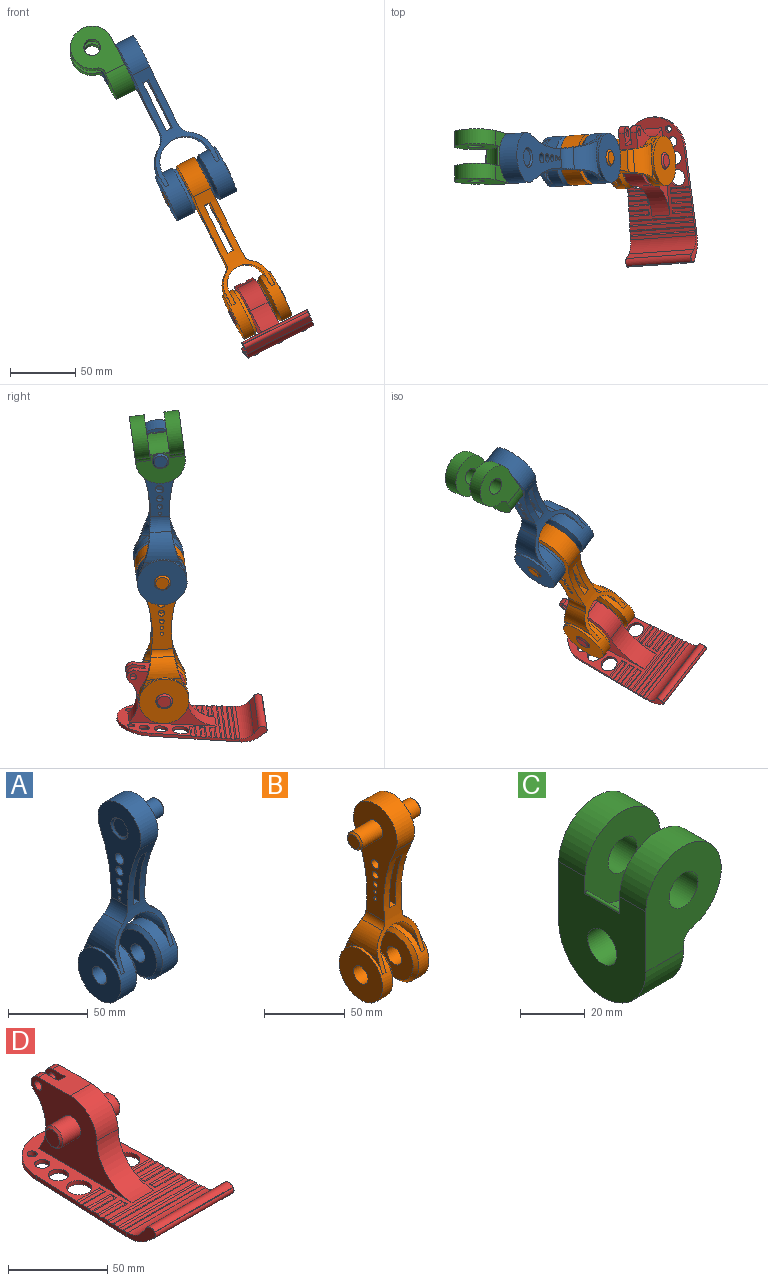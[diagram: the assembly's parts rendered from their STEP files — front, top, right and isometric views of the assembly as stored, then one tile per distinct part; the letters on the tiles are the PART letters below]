
ASSEMBLY  parts=4 mates=3
PART A: 47 faces, bbox 52.1x38.2x142.3 mm
  f0: cylinder r=101.6mm len=87.7mm, axis (-1,0,0), area 964.8mm2, adj f2,f3,f4,f5,f7,f12,f13,f14
  f1: cylinder r=101.6mm len=87.7mm, axis (-1,0,0), area 964.4mm2, adj f2,f3,f4,f5,f8,f9,f10,f11
  f2: cylinder r=23.61mm len=27.14mm, axis (0,1,0), area 470mm2, adj f0,f1,f5,f7,f11,f46
  f3: cylinder r=20.32mm len=40.64mm, axis (0,1,0), area 1216.7mm2, adj f0,f1,f5,f8,f9,f12,f13,f17
  f4: cylinder r=23.61mm len=27.14mm, axis (0,1,0), area 470mm2, adj f0,f1,f10,f14,f17,f45
  f5: cylinder r=19.05mm len=38.1mm, axis (-1,0,0), area 1536.5mm2, adj f0,f1,f2,f3,f7,f8,f11,f12
  f6: cylinder r=6.35mm len=16.51mm, axis (1,0,0), area 658.7mm2, adj f19,f21
  f7: plane 8.59x8.17mm, normal (-1,0,-0.04), area 11.2mm2, adj f0,f2,f5
  f8: plane 10.35x9.56mm, normal (1,0,0), area 16.7mm2, adj f1,f3,f5
  f9: plane 10.35x9.56mm, normal (-1,0,0), area 16.7mm2, adj f1,f3,f17
  f10: plane 8.59x8.17mm, normal (1,0,-0.04), area 11.2mm2, adj f1,f4,f17
  f11: plane 8.59x8.17mm, normal (-1,0,-0.04), area 11.2mm2, adj f1,f2,f5
  f12: plane 10.35x9.56mm, normal (1,0,0), area 16.7mm2, adj f0,f3,f5
  f13: plane 10.35x9.56mm, normal (-1,0,0), area 16.7mm2, adj f0,f3,f17
  f14: plane 8.59x8.17mm, normal (1,0,-0.04), area 11.2mm2, adj f0,f4,f17
  f15: plane 75.32x38.1mm, normal (1,0,0), area 1613mm2, adj f0,f1,f25,f26,f35,f36,f37,f38
  f16: plane 75.32x38.1mm, normal (-1,0,0), area 1557.2mm2, adj f0,f1,f25,f34,f40,f41,f42,f43
  f17: cylinder r=19.05mm len=38.1mm, axis (-1,0,0), area 1536.5mm2, adj f0,f1,f3,f4,f9,f10,f13,f14
  f18: plane 38.1x38.1mm, normal (1,0,0), area 1013.4mm2, adj f17,f20
  f19: plane 38.1x38.1mm, normal (-1,0,0), area 1013.4mm2, adj f5,f6
  f20: cylinder r=6.35mm len=16.51mm, axis (1,0,0), area 658.7mm2, adj f18,f22
  f21: plane 33.02x33.02mm, normal (1,0,0), area 729.7mm2, adj f6,f24
  f22: plane 33.02x33.02mm, normal (-1,0,0), area 729.7mm2, adj f20,f23
  f23: cone r=19.05mm half-angle=45deg, axis (1,0,0), area 401.3mm2, adj f17,f22
  f24: cone r=16.51mm half-angle=45deg, axis (-1,0,0), area 401.3mm2, adj f5,f21
  f25: cylinder r=19.05mm len=38.1mm, axis (-1,0,0), area 1171.2mm2, adj f0,f1,f15,f16
  f26: cylinder r=6.35mm len=17.78mm, axis (-1,0,0), area 709.4mm2, adj f15,f28
  f27: plane 10.16x10.16mm, normal (1,0,0), area 81.1mm2, adj f28
  f28: cone r=5.08mm half-angle=45deg, axis (-1,0,0), area 64.5mm2, adj f26,f27
  f29: plane 27.04x5.08mm, normal (0,0,-1), area 137.4mm2, adj f0,f1,f30,f32
  f30: plane 40.64x27.04mm, normal (1,0,0), area 620.1mm2, adj f0,f1,f29,f31,f40,f41,f42,f43
  f31: plane 14.77x5.08mm, normal (0,0,1), area 75mm2, adj f0,f1,f30,f32
  f32: plane 40.64x27.04mm, normal (-1,0,0), area 620.1mm2, adj f0,f1,f29,f31,f35,f36,f37,f38
  f33: plane 12.7x12.7mm, normal (-1,0,0), area 126.7mm2, adj f34
  f34: cone r=6.35mm half-angle=45deg, axis (-1,0,0), area 78.8mm2, adj f16,f33
  f35: cylinder r=2.54mm len=5.08mm, axis (1,0,0), area 81.1mm2, adj f15,f32
  f36: cylinder r=1.91mm len=5.08mm, axis (1,0,0), area 60.8mm2, adj f15,f32
  f37: cylinder r=1.27mm len=5.08mm, axis (1,0,0), area 40.5mm2, adj f15,f32
  f38: cylinder r=3.17mm len=6.35mm, axis (1,0,0), area 101.3mm2, adj f15,f32
  f39: cylinder r=3.81mm len=7.62mm, axis (1,0,0), area 121.6mm2, adj f15,f32
  f40: cylinder r=2.54mm len=5.08mm, axis (1,0,0), area 81.1mm2, adj f16,f30
  f41: cylinder r=1.91mm len=5.08mm, axis (1,0,0), area 60.8mm2, adj f16,f30
  f42: cylinder r=1.27mm len=5.08mm, axis (1,0,0), area 40.5mm2, adj f16,f30
  f43: cylinder r=3.17mm len=6.35mm, axis (1,0,0), area 101.3mm2, adj f16,f30
  f44: cylinder r=3.81mm len=7.62mm, axis (1,0,0), area 121.6mm2, adj f16,f30
  f45: cylinder r=12.7mm len=16.62mm, axis (0,1,0), area 192.8mm2, adj f0,f1,f4,f15
  f46: cylinder r=12.7mm len=16.62mm, axis (0,1,0), area 192.8mm2, adj f0,f1,f2,f16
PART B: 48 faces, bbox 53.3x38.1x142.2 mm
  f0: cylinder r=101.6mm len=87.7mm, axis (-1,0,0), area 975.1mm2, adj f2,f3,f4,f5,f6,f7,f13,f14
  f1: cylinder r=101.6mm len=87.7mm, axis (-1,0,0), area 974.7mm2, adj f2,f3,f4,f5,f6,f7,f9,f10
  f2: cylinder r=15.24mm len=30.48mm, axis (0,1,0), area 970.1mm2, adj f0,f1,f7,f9,f10,f13,f14,f19
  f3: cylinder r=18.41mm len=26.39mm, axis (0,1,0), area 372.4mm2, adj f0,f1,f5,f11,f15,f19
  f4: cylinder r=18.41mm len=26.39mm, axis (0,1,0), area 372.4mm2, adj f0,f1,f6,f7,f12,f18
  f5: cylinder r=6.35mm len=18.09mm, axis (0,1,0), area 106.3mm2, adj f0,f1,f3,f16
  f6: cylinder r=6.35mm len=18.09mm, axis (0,1,0), area 106.3mm2, adj f0,f1,f4,f17
  f7: cylinder r=19.05mm len=38.1mm, axis (-1,0,0), area 927.7mm2, adj f0,f1,f2,f4,f9,f12,f13,f18
  f8: cylinder r=6.35mm len=12.7mm, axis (1,0,0), area 456mm2, adj f21,f23
  f9: plane 10.35x9.56mm, normal (1,0,0), area 16.7mm2, adj f1,f2,f7
  f10: plane 10.35x9.56mm, normal (-1,0,0), area 16.7mm2, adj f1,f2,f19
  f11: plane 10.35x9.56mm, normal (1,0,0), area 16.7mm2, adj f1,f3,f19
  f12: plane 10.35x9.56mm, normal (-1,0,0), area 16.7mm2, adj f1,f4,f7
  f13: plane 10.35x9.56mm, normal (1,0,0), area 16.7mm2, adj f0,f2,f7
  f14: plane 10.35x9.56mm, normal (-1,0,0), area 16.7mm2, adj f0,f2,f19
  f15: plane 10.35x9.56mm, normal (1,0,0), area 16.7mm2, adj f0,f3,f19
  f16: plane 84.96x38.1mm, normal (1,0,0), area 1801.6mm2, adj f0,f1,f5,f27,f28,f37,f38,f39
  f17: plane 84.96x38.1mm, normal (-1,0,0), area 1801.6mm2, adj f0,f1,f6,f27,f35,f42,f43,f44
  f18: plane 10.35x9.56mm, normal (-1,0,0), area 16.7mm2, adj f0,f4,f7
  f19: cylinder r=19.05mm len=38.1mm, axis (-1,0,0), area 927.7mm2, adj f0,f1,f2,f3,f10,f11,f14,f15
  f20: plane 38.1x38.1mm, normal (1,0,0), area 1013.4mm2, adj f19,f22
  f21: plane 38.1x38.1mm, normal (-1,0,0), area 1013.4mm2, adj f7,f8
  f22: cylinder r=6.35mm len=12.7mm, axis (1,0,0), area 456mm2, adj f20,f24
  f23: plane 33.02x33.02mm, normal (1,0,0), area 729.7mm2, adj f8,f26
  f24: plane 33.02x33.02mm, normal (-1,0,0), area 729.7mm2, adj f22,f25
  f25: cone r=19.05mm half-angle=45deg, axis (1,0,0), area 401.3mm2, adj f19,f24
  f26: cone r=16.51mm half-angle=45deg, axis (-1,0,0), area 401.3mm2, adj f7,f23
  f27: cylinder r=19.05mm len=38.1mm, axis (-1,0,0), area 1171.2mm2, adj f0,f1,f16,f17
  f28: cylinder r=6.35mm len=17.78mm, axis (-1,0,0), area 709.4mm2, adj f16,f30
  f29: plane 10.16x10.16mm, normal (1,0,0), area 81.1mm2, adj f30
  f30: cone r=5.08mm half-angle=45deg, axis (-1,0,0), area 64.5mm2, adj f28,f29
  f31: plane 26.39x5.08mm, normal (0,0,-1), area 134.1mm2, adj f0,f1,f32,f34
  f32: plane 40.64x26.39mm, normal (1,0,0), area 650.1mm2, adj f0,f1,f31,f33,f42,f43,f44,f45
  f33: plane 14.87x5.08mm, normal (0,0,1), area 75.5mm2, adj f0,f1,f32,f34
  f34: plane 40.64x26.39mm, normal (-1,0,0), area 650.1mm2, adj f0,f1,f31,f33,f37,f38,f39,f40
  f35: cylinder r=6.35mm len=17.78mm, axis (1,0,0), area 709.4mm2, adj f17,f47
  f36: plane 10.16x10.16mm, normal (-1,0,0), area 81.1mm2, adj f47
  f37: cylinder r=1.91mm len=5.08mm, axis (1,0,0), area 60.8mm2, adj f16,f34
  f38: cylinder r=1.27mm len=5.08mm, axis (1,0,0), area 40.5mm2, adj f16,f34
  f39: cylinder r=1.27mm len=5.08mm, axis (1,0,0), area 40.5mm2, adj f16,f34
  f40: cylinder r=2.54mm len=5.08mm, axis (1,0,0), area 81.1mm2, adj f16,f34
  f41: cylinder r=3.17mm len=6.35mm, axis (1,0,0), area 101.3mm2, adj f16,f34
  f42: cylinder r=1.91mm len=5.08mm, axis (1,0,0), area 60.8mm2, adj f17,f32
  f43: cylinder r=1.27mm len=5.08mm, axis (1,0,0), area 40.5mm2, adj f17,f32
  f44: cylinder r=1.27mm len=5.08mm, axis (1,0,0), area 40.5mm2, adj f17,f32
  f45: cylinder r=2.54mm len=5.08mm, axis (1,0,0), area 81.1mm2, adj f17,f32
  f46: cylinder r=3.17mm len=6.35mm, axis (1,0,0), area 101.3mm2, adj f17,f32
  f47: cone r=5.08mm half-angle=45deg, axis (1,0,0), area 64.5mm2, adj f35,f36
PART C: 20 faces, bbox 33x38.1x58.4 mm
  f0: cylinder r=6.35mm len=12.7mm, axis (0,1,0), area 456mm2, adj f4,f11
  f1: cylinder r=16.51mm len=33.02mm, axis (0,1,0), area 844.4mm2, adj f4,f6,f11,f13
  f2: plane 38.1x24.9mm, normal (1,0,0), area 577.1mm2, adj f3,f4,f5,f7,f11,f12,f13,f14
  f3: cylinder r=19.05mm len=38.1mm, axis (-1,0,0), area 988.1mm2, adj f2,f4,f5,f6
  f4: plane 39.37x33.02mm, normal (0,1,0), area 896.7mm2, adj f0,f1,f2,f3,f6,f13
  f5: plane 39.37x33.02mm, normal (0,-1,0), area 896.7mm2, adj f2,f3,f6,f8,f9,f14
  f6: plane 41.91x38.1mm, normal (-1,0,0), area 1215.6mm2, adj f1,f3,f4,f5,f7,f9,f11,f12
  f7: cylinder r=6.35mm len=16.51mm, axis (1,0,0), area 658.7mm2, adj f2,f6,f15,f18
  f8: cylinder r=6.35mm len=12.7mm, axis (0,1,0), area 456mm2, adj f5,f12
  f9: cylinder r=16.51mm len=33.02mm, axis (0,1,0), area 844.4mm2, adj f5,f6,f12,f14
  f10: cylinder r=16.51mm len=15.29mm, axis (0,-1,0), area 291.5mm2, adj f11,f12,f15,f16,f17,f18,f19
  f11: plane 37.49x33.02mm, normal (0,-1,0), area 735.6mm2, adj f0,f1,f2,f6,f10,f13,f17,f19
  f12: plane 37.49x33.02mm, normal (0,1,0), area 735.6mm2, adj f2,f6,f8,f9,f10,f14,f16,f19
  f13: cylinder r=5.08mm len=11.43mm, axis (0,1,0), area 77.4mm2, adj f1,f2,f4,f11
  f14: cylinder r=5.08mm len=11.43mm, axis (0,1,0), area 77.4mm2, adj f2,f5,f9,f12
  f15: bspline ~2.72x0.6mm, area 0.6mm2, adj f7,f10,f16
  f16: cylinder r=0.51mm len=5.15mm, axis (0,-1,0), area 4mm2, adj f2,f10,f12,f15
  f17: cylinder r=0.51mm len=5.15mm, axis (0,-1,0), area 4mm2, adj f2,f10,f11,f18
  f18: bspline ~2.72x0.6mm, area 0.6mm2, adj f7,f10,f17
  f19: cylinder r=0.64mm len=15.24mm, axis (0,-1,0), area 26.7mm2, adj f6,f10,f11,f12
PART D: 97 faces, bbox 55.9x113x47.5 mm
  f0: plane 77.94x54.68mm, normal (0,0,1), area 2114.6mm2, adj f4,f8,f9,f22,f25,f26,f50,f52
  f1: plane 94.46x55.88mm, normal (0,0,-1), area 3970.7mm2, adj f2,f3,f8,f9,f10,f11,f16,f42
  f2: torus R=1.52mm, axis (0,0,-1), area 10.7mm2, adj f1,f39,f91
  f3: torus R=1.3mm, axis (0,0,1), area 5.1mm2, adj f1,f89
  f4: cylinder r=25.4mm len=35.06mm, axis (-1,0,0), area 575.1mm2, adj f0,f5,f23,f25,f26,f85,f86,f88
  f5: cylinder r=5.08mm len=8.92mm, axis (-1,0,0), area 62.7mm2, adj f4,f6,f26,f85
  f6: plane 22.72x15.24mm, normal (0,0,1), area 300.4mm2, adj f5,f23,f24,f25,f26,f85,f86,f87
  f7: cylinder r=2.54mm len=5.08mm, axis (1,0,0), area 81.1mm2, adj f26,f85
  f8: plane 67.32x2.77mm, normal (-1,0.04,0), area 163.1mm2, adj f0,f1,f11,f12,f17,f51,f53,f54
  f9: plane 67.32x2.77mm, normal (1,0.04,0), area 163.1mm2, adj f0,f1,f10,f12,f17,f54,f55,f59
  f10: plane 20.5x14.03mm, normal (1,0,0), area 103.9mm2, adj f1,f9,f13,f14,f15,f16,f17,f18
  f11: plane 20.5x14.03mm, normal (-1,0,0), area 103.9mm2, adj f1,f8,f13,f14,f15,f16,f17,f18
  f12: plane 55.31x3.05mm, normal (0,0,1), area 168.2mm2, adj f8,f9,f66,f69
  f13: plane 55.88x0.12mm, normal (0,-0.77,0.64), area 8.4mm2, adj f10,f11,f14,f20
  f14: cylinder r=2.54mm len=55.88mm, axis (-1,0,0), area 223mm2, adj f10,f11,f13,f15
  f15: plane 55.88x5.39mm, normal (0,-0.64,-0.77), area 393.2mm2, adj f10,f11,f14,f16
  f16: cylinder r=19.05mm len=55.88mm, axis (-1,0,0), area 743.2mm2, adj f1,f10,f11,f15
  f17: plane 55.88x2.62mm, normal (0,0,1), area 146.3mm2, adj f8,f9,f10,f11,f18,f68
  f18: cylinder r=12.7mm len=55.88mm, axis (-1,0,0), area 681.2mm2, adj f10,f11,f17,f19
  f19: plane 55.88x4.45mm, normal (0,0.82,0.57), area 303.8mm2, adj f10,f11,f18,f20
  f20: cylinder r=3.81mm len=55.88mm, axis (-1,0,0), area 390.2mm2, adj f10,f11,f13,f19
  f21: cylinder r=26.05mm len=25.39mm, axis (-1,0,0), area 600.5mm2, adj f22,f24,f25,f26
  f22: plane 24.51x15.24mm, normal (0,0,-1), area 373.6mm2, adj f0,f21,f25,f26
  f23: cylinder r=5.08mm len=8.92mm, axis (-1,0,0), area 62.7mm2, adj f4,f6,f25,f86
  f24: cylinder r=19.05mm len=19.04mm, axis (-1,0,0), area 448.8mm2, adj f6,f21,f25,f26
  f25: plane 72.02x43.98mm, normal (1,0,0), area 1683.5mm2, adj f0,f4,f6,f21,f22,f23,f24,f27
  f26: plane 72.02x43.98mm, normal (-1,0,0), area 1683.5mm2, adj f0,f4,f5,f6,f7,f21,f22,f24
  f27: cylinder r=6.35mm len=12.7mm, axis (-1,0,0), area 506.7mm2, adj f25,f32
  f28: plane 10.16x10.16mm, normal (1,0,0), area 81.1mm2, adj f32
  f29: cylinder r=6.35mm len=12.7mm, axis (1,0,0), area 506.7mm2, adj f26,f31
  f30: plane 10.16x10.16mm, normal (-1,0,0), area 81.1mm2, adj f31
  f31: cone r=6.35mm half-angle=45deg, axis (1,0,0), area 64.5mm2, adj f29,f30
  f32: cone r=5.08mm half-angle=45deg, axis (-1,0,0), area 64.5mm2, adj f27,f28
  f33: plane 2.44x2.22mm, normal (0,0,-1), area 2.2mm2, adj f42,f92
  f34: plane 3.05x3.05mm, normal (0,0,-1), area 7.3mm2, adj f49
  f35: plane 3.05x3.05mm, normal (0,0,-1), area 7.3mm2, adj f48
  f36: plane 3.05x3.05mm, normal (0,0,-1), area 7.3mm2, adj f47
  f37: plane 3.05x3.05mm, normal (0,0,-1), area 7.3mm2, adj f46
  f38: plane 3.05x3.05mm, normal (0,0,-1), area 7.3mm2, adj f45
  f39: plane 2.44x2.22mm, normal (0,0,-1), area 2.2mm2, adj f2,f91
  f40: plane 3.05x3.05mm, normal (0,0,-1), area 7.3mm2, adj f44
  f41: plane 3.05x3.05mm, normal (0,0,-1), area 7.3mm2, adj f43
  f42: torus R=1.52mm, axis (0,0,-1), area 10.7mm2, adj f1,f33,f92
  f43: torus R=1.52mm, axis (0,0,-1), area 21.8mm2, adj f1,f41
  f44: torus R=1.52mm, axis (0,0,-1), area 21.8mm2, adj f1,f40
  f45: torus R=1.52mm, axis (0,0,-1), area 21.8mm2, adj f1,f38
  f46: torus R=1.52mm, axis (0,0,-1), area 21.8mm2, adj f1,f37
  f47: torus R=1.52mm, axis (0,0,-1), area 21.8mm2, adj f1,f36
  f48: torus R=1.52mm, axis (0,0,-1), area 21.8mm2, adj f1,f35
  f49: torus R=1.52mm, axis (0,0,-1), area 21.8mm2, adj f1,f34
  f50: plane 4.57x0.51mm, normal (-1,0,0), area 1.6mm2, adj f0,f51,f76,f77
  f51: plane 16.7x2.54mm, normal (0,0,1), area 42.3mm2, adj f8,f50,f76,f77
  f52: plane 4.57x0.51mm, normal (-1,0,0), area 1.6mm2, adj f0,f53,f72,f73
  f53: plane 16.39x2.54mm, normal (0,0,1), area 41.5mm2, adj f8,f52,f72,f73
  f54: plane 55.6x2.54mm, normal (0,0,1), area 141mm2, adj f8,f9,f68,f69
  f55: plane 54.98x2.54mm, normal (0,0,1), area 139.4mm2, adj f8,f9,f66,f67
  f56: plane 4.57x0.51mm, normal (-1,0,0), area 1.6mm2, adj f0,f57,f64,f65
  f57: plane 17.01x2.54mm, normal (0,0,1), area 43.1mm2, adj f8,f56,f64,f65
  f58: plane 4.57x0.51mm, normal (1,0,0), area 1.6mm2, adj f0,f59,f78,f79
  f59: plane 17.01x2.54mm, normal (0,0,1), area 43.1mm2, adj f9,f58,f78,f79
  f60: plane 4.57x0.51mm, normal (1,0,0), area 1.6mm2, adj f0,f61,f74,f75
  f61: plane 16.7x2.54mm, normal (0,0,1), area 42.3mm2, adj f9,f60,f74,f75
  f62: plane 4.57x0.51mm, normal (1,0,0), area 1.6mm2, adj f0,f63,f70,f71
  f63: plane 16.39x2.54mm, normal (0,0,1), area 41.5mm2, adj f9,f62,f70,f71
  f64: cylinder r=1.27mm len=17.06mm, axis (-1,0,0), area 20.1mm2, adj f0,f8,f56,f57
  f65: cylinder r=1.27mm len=16.91mm, axis (-1,0,0), area 19.9mm2, adj f0,f8,f56,f57
  f66: cylinder r=1.27mm len=55.06mm, axis (-1,0,0), area 64.8mm2, adj f8,f9,f12,f55
  f67: cylinder r=1.27mm len=54.77mm, axis (-1,0,0), area 64.4mm2, adj f0,f8,f9,f55
  f68: cylinder r=1.27mm len=55.69mm, axis (-1,0,0), area 65.5mm2, adj f8,f9,f17,f54
  f69: cylinder r=1.27mm len=55.39mm, axis (-1,0,0), area 65.2mm2, adj f8,f9,f12,f54
  f70: cylinder r=1.27mm len=16.43mm, axis (-1,0,0), area 19.3mm2, adj f0,f9,f62,f63
  f71: cylinder r=1.27mm len=16.28mm, axis (-1,0,0), area 19.2mm2, adj f0,f9,f62,f63
  f72: cylinder r=1.27mm len=16.43mm, axis (-1,0,0), area 19.3mm2, adj f0,f8,f52,f53
  f73: cylinder r=1.27mm len=16.28mm, axis (-1,0,0), area 19.2mm2, adj f0,f8,f52,f53
  f74: cylinder r=1.27mm len=16.74mm, axis (-1,0,0), area 19.7mm2, adj f0,f9,f60,f61
  f75: cylinder r=1.27mm len=16.6mm, axis (-1,0,0), area 19.5mm2, adj f0,f9,f60,f61
  f76: cylinder r=1.27mm len=16.74mm, axis (-1,0,0), area 19.7mm2, adj f0,f8,f50,f51
  f77: cylinder r=1.27mm len=16.6mm, axis (-1,0,0), area 19.5mm2, adj f0,f8,f50,f51
  f78: cylinder r=1.27mm len=17.06mm, axis (-1,0,0), area 20.1mm2, adj f0,f9,f58,f59
  f79: cylinder r=1.27mm len=16.91mm, axis (-1,0,0), area 19.9mm2, adj f0,f9,f58,f59
  f80: plane 2.54x0.02mm, normal (0,-1,0), area 0mm2, adj f0,f1,f8,f82
  f81: plane 2.54x0.02mm, normal (0,-1,0), area 0mm2, adj f0,f1,f9,f82
  f82: cylinder r=25.19mm len=50.38mm, axis (0,0,-1), area 201mm2, adj f0,f1,f80,f81
  f83: torus R=1.3mm, axis (0,0,1), area 5.1mm2, adj f1,f90
  f84: cylinder r=2.54mm len=5.08mm, axis (1,0,0), area 81.1mm2, adj f25,f86
  f85: plane 14.13x11.43mm, normal (1,0,0), area 95.1mm2, adj f4,f5,f6,f7,f87,f88
  f86: plane 14.13x11.43mm, normal (-1,0,0), area 95.1mm2, adj f4,f6,f23,f84,f87,f88
  f87: plane 7.56x5.08mm, normal (0,0.92,0.39), area 41.7mm2, adj f6,f85,f86,f88
  f88: cylinder r=6.35mm len=6.7mm, axis (1,0,0), area 42.1mm2, adj f4,f85,f86,f87
  f89: cylinder r=2.54mm len=5.08mm, axis (0,0,1), area 44.6mm2, adj f0,f1,f3
  f90: cylinder r=2.54mm len=5.08mm, axis (0,0,1), area 44.6mm2, adj f0,f1,f83
  f91: cylinder r=5.08mm len=10.16mm, axis (0,0,1), area 86mm2, adj f0,f1,f2,f39
  f92: cylinder r=5.08mm len=10.16mm, axis (0,0,1), area 86mm2, adj f0,f1,f33,f42
  f93: cylinder r=6.35mm len=12.7mm, axis (0,0,1), area 101.3mm2, adj f0,f1
  f94: cylinder r=3.81mm len=7.62mm, axis (0,0,1), area 60.8mm2, adj f0,f1
  f95: cylinder r=6.35mm len=12.7mm, axis (0,0,1), area 101.3mm2, adj f0,f1
  f96: cylinder r=3.81mm len=7.62mm, axis (0,0,1), area 60.8mm2, adj f0,f1
PLACE A rot(axis=(0.23,-0.01,-0.97),176.7deg) t=(219.51,1.64,-99.53)mm
PLACE B rot(axis=(-0.07,-0.99,0.12),26.9deg) t=(288.86,1.94,-181.26)mm
PLACE C rot(axis=(0.23,-0.07,-0.97),178.1deg) t=(209.2,4.44,-79.32)mm fixed
PLACE D rot(axis=(0.14,-0.98,0.17),27.1deg) t=(335.57,0.19,-274.32)mm
MATE revolute A.f25 <-> C.f3  axis (-0.89,-0.06,-0.45) through (219.51,1.64,-99.53)mm
MATE revolute B.f8 <-> D.f27  axis (0.89,0.06,0.45) through (353.71,1.46,-265.25)mm
MATE revolute B.f27 <-> A.f5  axis (0.89,0.06,0.45) through (311.53,3.53,-169.91)mm
